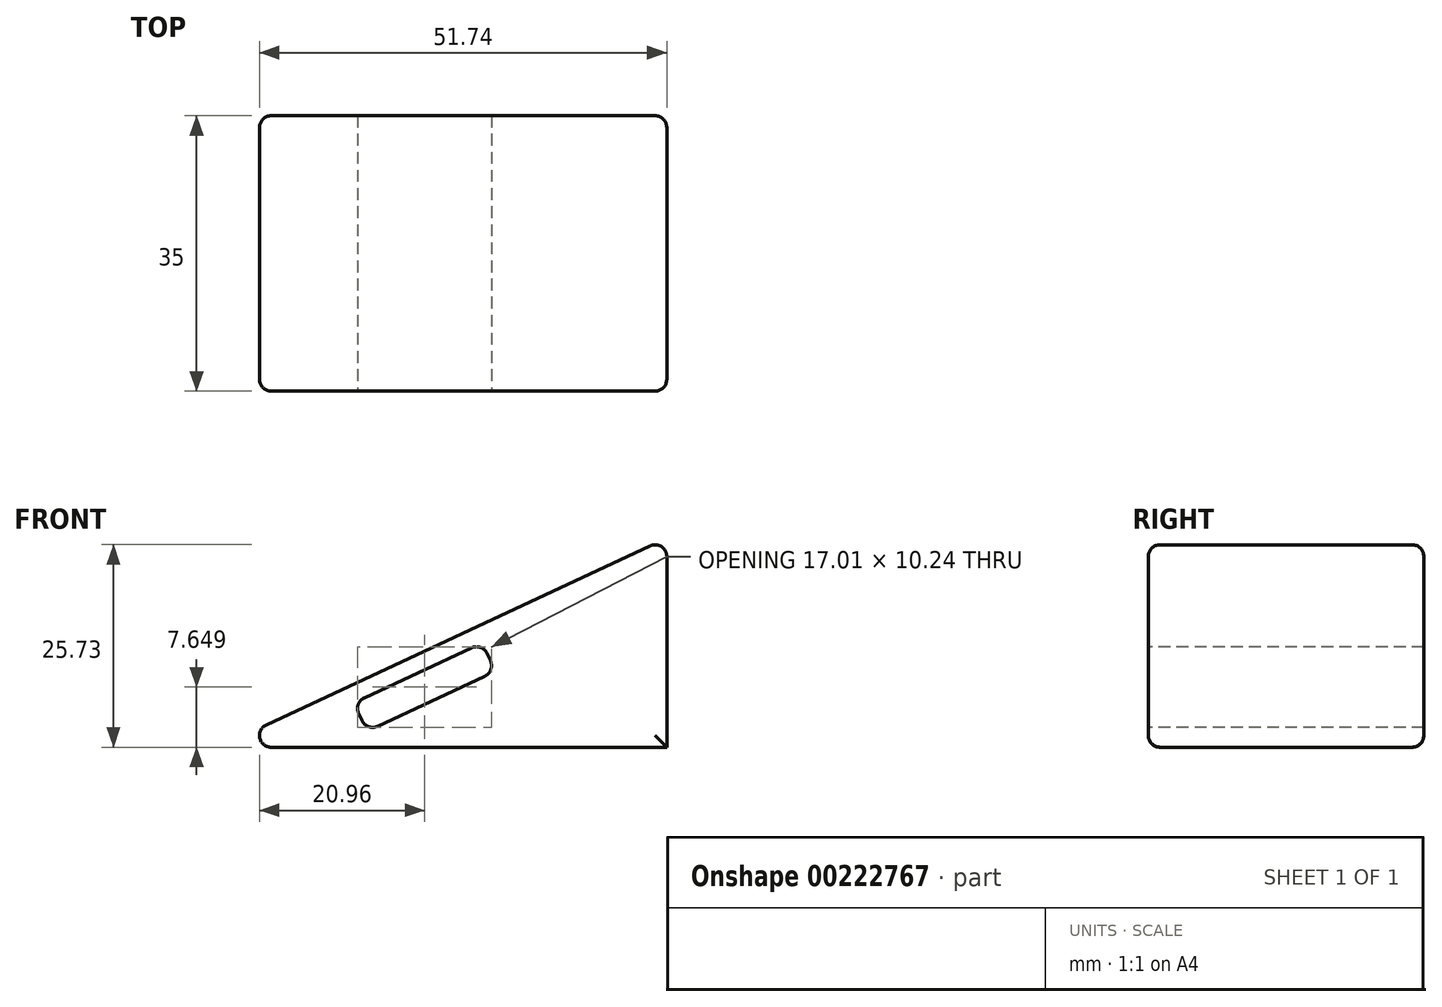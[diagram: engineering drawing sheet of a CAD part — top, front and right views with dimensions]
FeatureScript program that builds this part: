
annotation { "Feature Type Name" : "Feature", "Feature Type Description" : "" }
export const myFeature = defineFeature(function(context is Context, id is Id, definition is map)
    precondition{}
    {
        {
            var Q0;
            Q0=qCreatedBy(makeId("Front.planeOp"),FACE);
            var sketch = newSketch(context, id + "F0", { "sketchPlane" : qUnion([Q0])});
            skLineSegment(sketch, "E0", {"start": v(-25.92, 0) * mm, "end": v(31.08, 0) * mm});
            skLineSegment(sketch, "E1", {"start": v(-25.92, 0) * mm, "end": v(26.04, 24.23) * mm});
            skLineSegment(sketch, "E2", {"start": v(31.08, 0) * mm, "end": v(31.08, 26.58) * mm});
            skLineSegment(sketch, "E3", {"start": v(26.04, 24.23) * mm, "end": v(31.08, 26.58) * mm});
            skSolve(sketch);
        }
        {
            var Q0;
            Q0=makeQuery(id+"F0.imprint","IMPRINT",FACE,{"disambiguationData":[TD([[makeQuery(id+"F0.imprint","IMPRINT",EDGE,{"derivedFrom":sQuery(id+"F0.wireOp",EDGE,"E0")}),1.0]])]});
            extrude(context, id + "F1", {"entities" : qUnion([Q0]), "depth" : 35 * mm});
        }
        {
            var Q0;
            Q0=makeQuery(id+"F1.opExtrude","CAP_FACE",FACE,{"disambiguationData":[OSD([sQuery(id+"F0.wireOp",EDGE,"E0"),sQuery(id+"F0.wireOp",EDGE,"E1"),sQuery(id+"F0.wireOp",EDGE,"E2"),sQuery(id+"F0.wireOp",EDGE,"E3")])],"isStart":false});
            var sketch = newSketch(context, id + "F2", { "sketchPlane" : qUnion([Q0])});
            skLineSegment(sketch, "E4", {"start": v(-25.92, 0) * mm, "end": v(-9.61, 7.6) * mm, "construction": true});
            skLineSegment(sketch, "E5", {"start": v(-8.07, 4.3) * mm, "end": v(-7.64, 3.4) * mm, "construction": true});
            skPoint(sketch, "E6", {"position": v(-8.7, 5.66) * mm});
            skLineSegment(sketch, "E7", {"start": v(-7.34, 6.3) * mm, "end": v(6.25, 12.63) * mm});
            skLineSegment(sketch, "E8", {"start": v(8.25, 11.9) * mm, "end": v(8.67, 11) * mm});
            skLineSegment(sketch, "E9", {"start": v(7.94, 9) * mm, "end": v(-5.65, 2.67) * mm});
            skLineSegment(sketch, "E10", {"start": v(-7.01, 2.03) * mm, "end": v(-8.7, 5.66) * mm});
            skPoint(sketch, "E11.visualSharp", {"position": v(7.61, 13.27) * mm});
            skArc(sketch, "E11.filletArc", {"start": v(8.25, 11.9) * mm, "mid": v(7.4, 12.68) * mm, "end": v(6.25, 12.63) * mm});
            skPoint(sketch, "E12.visualSharp", {"position": v(9.3, 9.64) * mm});
            skArc(sketch, "E12.filletArc", {"start": v(7.94, 9) * mm, "mid": v(8.72, 9.85) * mm, "end": v(8.67, 11) * mm});
            skPoint(sketch, "E13.newPointB", {"position": v(-9.61, 7.6) * mm});
            skArc(sketch, "E13.filletArc", {"start": v(-7.34, 6.3) * mm, "mid": v(-8.12, 5.45) * mm, "end": v(-8.07, 4.3) * mm});
            skPoint(sketch, "E14.newPointA", {"position": v(-7.01, 2.03) * mm});
            skPoint(sketch, "E14.newPointB", {"position": v(-6.06, 0) * mm});
            skArc(sketch, "E14.filletArc", {"start": v(-7.64, 3.4) * mm, "mid": v(-6.8, 2.62) * mm, "end": v(-5.65, 2.67) * mm});
            skSolve(sketch);
        }
        {
            var Q0;
            Q0=makeQuery(id+"F2.imprint","IMPRINT",FACE,{"disambiguationData":[TD([[makeQuery(id+"F2.imprint","IMPRINT",EDGE,{"derivedFrom":sQuery(id+"F2.wireOp",EDGE,"E7")}),-1.0]])]});
            extrude(context, id + "F3", {"entities" : qUnion([Q0]), "operationType" : NewBodyOperationType.REMOVE, "endBound" : BoundingType.THROUGH_ALL, "oppositeDirection" : true, "depth" : 25 * mm});
        }
        {
            var Q0;
            Q0=makeQuery(id+"F1.opExtrude","SWEPT_EDGE",EDGE,{"disambiguationData":[OSD([sQuery(id+"F0.wireOp",EDGE,"E0"),sQuery(id+"F0.wireOp",EDGE,"E1")])]});
            var Q1;
            Q1=makeQuery(id+"F1.opExtrude","SWEPT_EDGE",EDGE,{"disambiguationData":[OSD([sQuery(id+"F0.wireOp",EDGE,"E2"),sQuery(id+"F0.wireOp",EDGE,"E3")])]});
            fillet(context, id + "F4", {"entities" : qUnion([Q0, Q1]), "radius" : 1.5 * mm, "tangentPropagation" : true, "allowEdgeOverflow" : false});
        }
        {
            var Q0;
            Q0=makeQuery(id+"F1.opExtrude","CAP_EDGE",EDGE,{"disambiguationData":[OSD([sQuery(id+"F0.wireOp",EDGE,"E2")])],"isStart":false});
            var Q1;
            Q1=makeQuery(id+"F1.opExtrude","CAP_EDGE",EDGE,{"disambiguationData":[OSD([sQuery(id+"F0.wireOp",EDGE,"E2")])],"isStart":true});
            fillet(context, id + "F5", {"entities" : qUnion([Q0, Q1]), "radius" : 1.5 * mm, "tangentPropagation" : true, "allowEdgeOverflow" : false});
        }
    });
